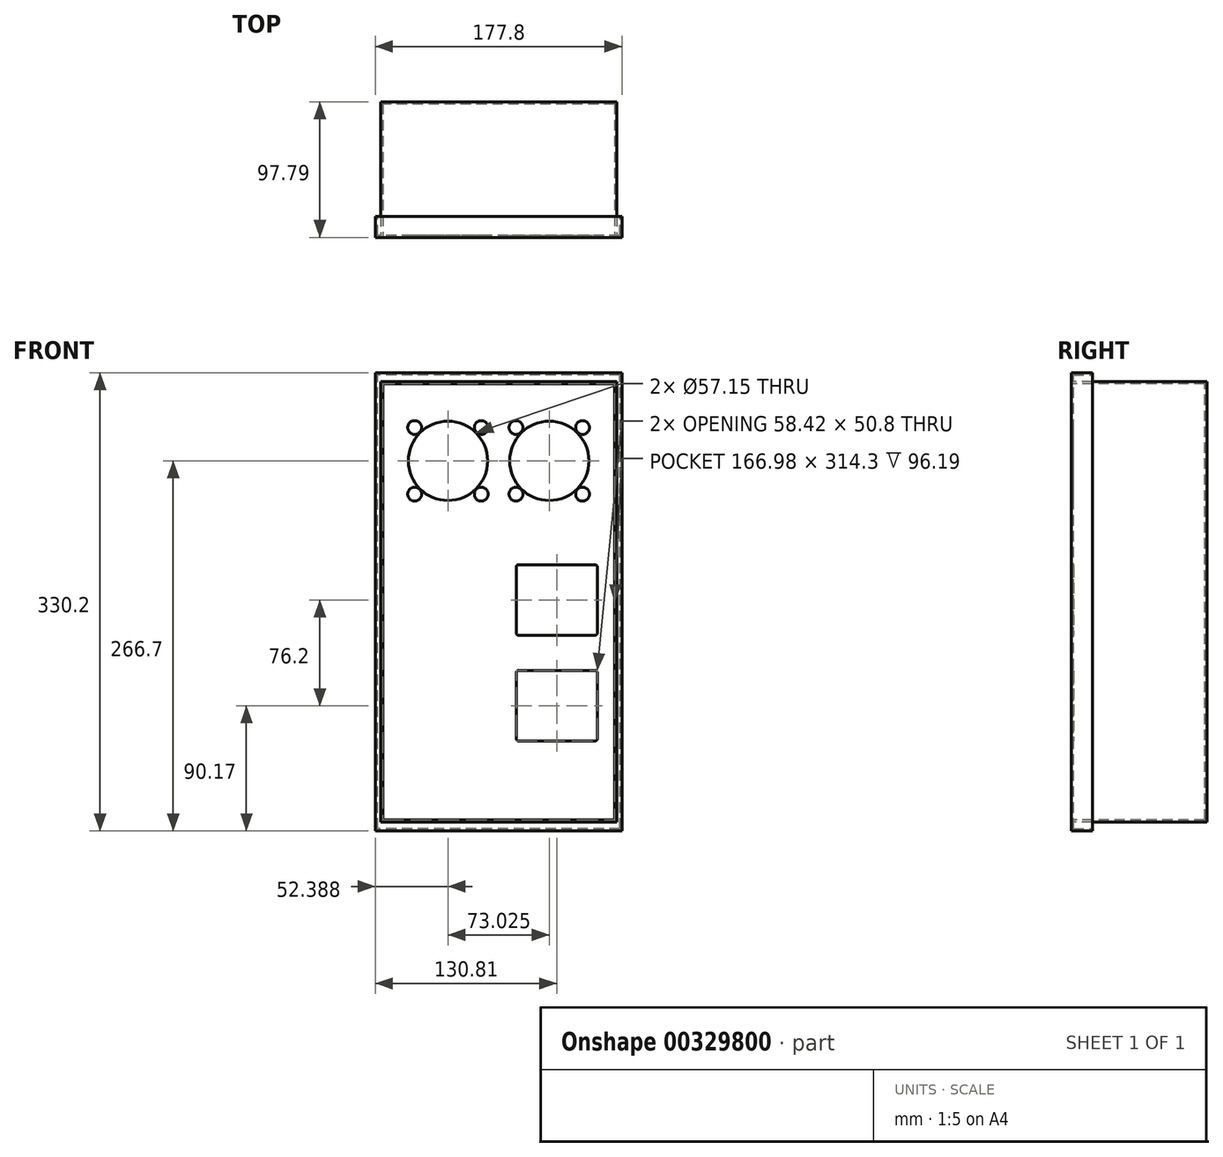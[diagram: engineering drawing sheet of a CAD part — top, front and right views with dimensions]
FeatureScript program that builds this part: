
annotation { "Feature Type Name" : "Feature", "Feature Type Description" : "" }
export const myFeature = defineFeature(function(context is Context, id is Id, definition is map)
    precondition{}
    {
        {
            var Q0;
            Q0=qCreatedBy(makeId("Front.planeOp"),FACE);
            var sketch = newSketch(context, id + "F0", { "sketchPlane" : qUnion([Q0])});
            skLineSegment(sketch, "E0.bottom", {"start": v(0, 0) * mm, "end": v(-177.8, 0) * mm});
            skLineSegment(sketch, "E0.top", {"start": v(0, 330.2) * mm, "end": v(-177.8, 330.2) * mm});
            skLineSegment(sketch, "E0.left", {"start": v(0, 0) * mm, "end": v(0, 330.2) * mm});
            skLineSegment(sketch, "E0.right", {"start": v(-177.8, 0) * mm, "end": v(-177.8, 330.2) * mm});
            skSolve(sketch);
        }
        {
            var Q0;
            Q0 = qSketchRegion(id + "F0", true);
            extrude(context, id + "F1", {"entities" : qUnion([Q0]), "depth" : 15.24 * mm});
        }
        {
            var Q0;
            Q0=makeQuery(id+"F1.opExtrude","CAP_FACE",FACE,{"disambiguationData":[OSD([sQuery(id+"F0.wireOp",EDGE,"E0.bottom"),sQuery(id+"F0.wireOp",EDGE,"E0.top"),sQuery(id+"F0.wireOp",EDGE,"E0.left"),sQuery(id+"F0.wireOp",EDGE,"E0.right")])],"isStart":true});
            shell(context, id + "F2", {"entities" : qUnion([Q0]), "thickness" : 1.6 * mm});
        }
        {
            var Q0;
            Q0=makeQuery(id+"F1.opExtrude","CAP_FACE",FACE,{"disambiguationData":[OSD([sQuery(id+"F0.wireOp",EDGE,"E0.bottom"),sQuery(id+"F0.wireOp",EDGE,"E0.top"),sQuery(id+"F0.wireOp",EDGE,"E0.left"),sQuery(id+"F0.wireOp",EDGE,"E0.right")])],"isStart":false});
            var sketch = newSketch(context, id + "F3", { "sketchPlane" : qUnion([Q0])});
            skLineSegment(sketch, "E1.bottom", {"start": v(-74.61, 115.57) * mm, "end": v(-19.37, 115.57) * mm});
            skLineSegment(sketch, "E1.top", {"start": v(-74.61, 64.77) * mm, "end": v(-19.37, 64.77) * mm});
            skLineSegment(sketch, "E1.left", {"start": v(-76.2, 113.98) * mm, "end": v(-76.2, 66.36) * mm});
            skLineSegment(sketch, "E1.right", {"start": v(-17.78, 113.98) * mm, "end": v(-17.78, 66.36) * mm});
            skLineSegment(sketch, "E2.bottom", {"start": v(-74.61, 191.77) * mm, "end": v(-19.37, 191.77) * mm});
            skLineSegment(sketch, "E2.top", {"start": v(-74.61, 140.97) * mm, "end": v(-19.37, 140.97) * mm});
            skLineSegment(sketch, "E2.left", {"start": v(-76.2, 190.18) * mm, "end": v(-76.2, 142.56) * mm});
            skLineSegment(sketch, "E2.right", {"start": v(-17.78, 190.18) * mm, "end": v(-17.78, 142.56) * mm});
            skPoint(sketch, "E3.visualSharp", {"position": v(-17.78, 191.77) * mm});
            skArc(sketch, "E3.filletArc", {"start": v(-17.78, 190.18) * mm, "mid": v(-18.24, 191.3) * mm, "end": v(-19.37, 191.77) * mm});
            skPoint(sketch, "E4.visualSharp", {"position": v(-76.2, 191.77) * mm});
            skArc(sketch, "E4.filletArc", {"start": v(-74.61, 191.77) * mm, "mid": v(-75.74, 191.3) * mm, "end": v(-76.2, 190.18) * mm});
            skPoint(sketch, "E5.visualSharp", {"position": v(-76.2, 140.97) * mm});
            skArc(sketch, "E5.filletArc", {"start": v(-76.2, 142.56) * mm, "mid": v(-75.74, 141.43) * mm, "end": v(-74.61, 140.97) * mm});
            skPoint(sketch, "E6.visualSharp", {"position": v(-17.78, 140.97) * mm});
            skArc(sketch, "E6.filletArc", {"start": v(-19.37, 140.97) * mm, "mid": v(-18.24, 141.43) * mm, "end": v(-17.78, 142.56) * mm});
            skPoint(sketch, "E7.visualSharp", {"position": v(-17.78, 115.57) * mm});
            skArc(sketch, "E7.filletArc", {"start": v(-17.78, 113.98) * mm, "mid": v(-18.24, 115.1) * mm, "end": v(-19.37, 115.57) * mm});
            skPoint(sketch, "E8.visualSharp", {"position": v(-76.2, 115.57) * mm});
            skArc(sketch, "E8.filletArc", {"start": v(-74.61, 115.57) * mm, "mid": v(-75.74, 115.1) * mm, "end": v(-76.2, 113.98) * mm});
            skPoint(sketch, "E9.visualSharp", {"position": v(-76.2, 64.77) * mm});
            skArc(sketch, "E9.filletArc", {"start": v(-76.2, 66.36) * mm, "mid": v(-75.74, 65.23) * mm, "end": v(-74.61, 64.77) * mm});
            skPoint(sketch, "E10.visualSharp", {"position": v(-17.78, 64.77) * mm});
            skArc(sketch, "E10.filletArc", {"start": v(-19.37, 64.77) * mm, "mid": v(-18.24, 65.23) * mm, "end": v(-17.78, 66.36) * mm});
            skSolve(sketch);
        }
        {
            var Q0;
            Q0 = qSketchRegion(id + "F3", true);
            extrude(context, id + "F4", {"entities" : qUnion([Q0]), "operationType" : NewBodyOperationType.REMOVE, "endBound" : BoundingType.THROUGH_ALL, "oppositeDirection" : true, "depth" : 25.4 * mm});
        }
        {
            var Q0;
            Q0=makeQuery(id+"F1.opExtrude","CAP_FACE",FACE,{"disambiguationData":[OSD([sQuery(id+"F0.wireOp",EDGE,"E0.bottom"),sQuery(id+"F0.wireOp",EDGE,"E0.top"),sQuery(id+"F0.wireOp",EDGE,"E0.left"),sQuery(id+"F0.wireOp",EDGE,"E0.right")])],"isStart":false});
            var sketch = newSketch(context, id + "F5", { "sketchPlane" : qUnion([Q0])});
            skCircle(sketch, "E11", {"center": v(-125.41, 266.7) * mm, "radius": 28.58 * mm});
            skCircle(sketch, "E12", {"center": v(-52.39, 266.7) * mm, "radius": 28.58 * mm});
            skLineSegment(sketch, "E13.bottom", {"start": v(-92.4, 233.68) * mm, "end": v(-158.43, 233.68) * mm, "construction": true});
            skLineSegment(sketch, "E13.top", {"start": v(-92.4, 299.72) * mm, "end": v(-158.43, 299.72) * mm, "construction": true});
            skLineSegment(sketch, "E13.left", {"start": v(-92.4, 233.68) * mm, "end": v(-92.4, 299.72) * mm, "construction": true});
            skLineSegment(sketch, "E13.right", {"start": v(-158.43, 233.68) * mm, "end": v(-158.43, 299.72) * mm, "construction": true});
            skLineSegment(sketch, "E14.bottom", {"start": v(-19.37, 233.68) * mm, "end": v(-85.4, 233.68) * mm, "construction": true});
            skLineSegment(sketch, "E14.top", {"start": v(-19.37, 299.72) * mm, "end": v(-85.4, 299.72) * mm, "construction": true});
            skLineSegment(sketch, "E14.left", {"start": v(-19.37, 233.68) * mm, "end": v(-19.37, 299.72) * mm, "construction": true});
            skLineSegment(sketch, "E14.right", {"start": v(-85.4, 233.68) * mm, "end": v(-85.4, 299.72) * mm, "construction": true});
            skCircle(sketch, "E15", {"center": v(-149.41, 290.7) * mm, "radius": 5 * mm});
            skCircle(sketch, "E16", {"center": v(-101.41, 290.7) * mm, "radius": 5 * mm});
            skCircle(sketch, "E17", {"center": v(-76.39, 290.7) * mm, "radius": 5 * mm});
            skCircle(sketch, "E18", {"center": v(-28.39, 290.7) * mm, "radius": 5 * mm});
            skCircle(sketch, "E19", {"center": v(-28.39, 242.7) * mm, "radius": 5 * mm});
            skCircle(sketch, "E20", {"center": v(-76.39, 242.7) * mm, "radius": 5 * mm});
            skCircle(sketch, "E21", {"center": v(-101.41, 242.7) * mm, "radius": 5 * mm});
            skCircle(sketch, "E22", {"center": v(-149.41, 242.7) * mm, "radius": 5 * mm});
            skSolve(sketch);
        }
        {
            var Q0;
            Q0 = qSketchRegion(id + "F5", true);
            extrude(context, id + "F6", {"entities" : qUnion([Q0]), "operationType" : NewBodyOperationType.REMOVE, "endBound" : BoundingType.THROUGH_ALL, "oppositeDirection" : true, "depth" : 25.4 * mm});
        }
        {
            var Q0;
            Q0=qCreatedBy(makeId("Front.planeOp"),FACE);
            var sketch = newSketch(context, id + "F7", { "sketchPlane" : qUnion([Q0])});
            skLineSegment(sketch, "E23.bottom", {"start": v(-3.8, 6.35) * mm, "end": v(-174, 6.35) * mm});
            skLineSegment(sketch, "E23.top", {"start": v(-3.8, 323.85) * mm, "end": v(-174, 323.85) * mm});
            skLineSegment(sketch, "E23.left", {"start": v(-3.8, 6.35) * mm, "end": v(-3.8, 323.85) * mm});
            skLineSegment(sketch, "E23.right", {"start": v(-174, 6.35) * mm, "end": v(-174, 323.85) * mm});
            skSolve(sketch);
        }
        {
            var Q0;
            Q0 = qSketchRegion(id + "F7", true);
            extrude(context, id + "F8", {"entities" : qUnion([Q0]), "oppositeDirection" : true, "depth" : 82.55 * mm, "hasSecondDirection" : true, "secondDirectionOppositeDirection" : false, "secondDirectionDepth" : 15.24 * mm});
        }
        {
            var Q0;
            Q0=makeQuery(id+"F8.opExtrude","CAP_FACE",FACE,{"disambiguationData":[OSD([sQuery(id+"F7.wireOp",EDGE,"E23.bottom"),sQuery(id+"F7.wireOp",EDGE,"E23.top"),sQuery(id+"F7.wireOp",EDGE,"E23.left"),sQuery(id+"F7.wireOp",EDGE,"E23.right")])],"isStart":true});
            shell(context, id + "F9", {"entities" : qUnion([Q0]), "thickness" : 1.6 * mm});
        }
    });
